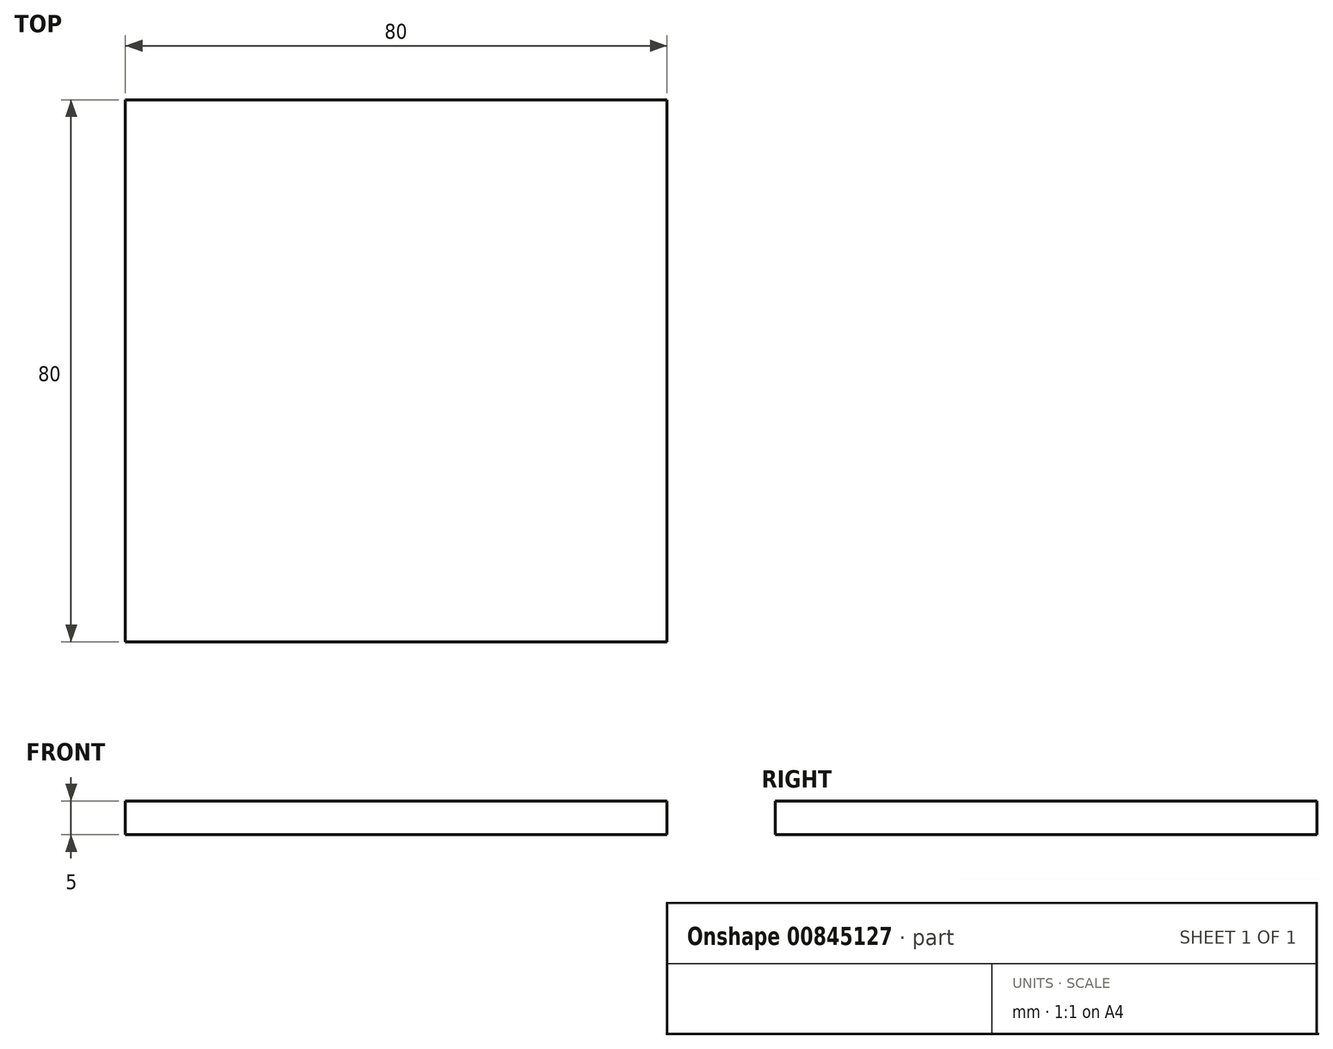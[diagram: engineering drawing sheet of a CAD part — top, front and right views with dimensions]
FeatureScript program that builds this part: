
annotation { "Feature Type Name" : "Feature", "Feature Type Description" : "" }
export const myFeature = defineFeature(function(context is Context, id is Id, definition is map)
    precondition{}
    {
        {
            var Q0;
            Q0=qCreatedBy(makeId("Top.planeOp"),FACE);
            var sketch = newSketch(context, id + "F0", { "sketchPlane" : qUnion([Q0])});
            skLineSegment(sketch, "E0.bottom", {"start": v(0, 0) * mm, "end": v(80, 0) * mm});
            skLineSegment(sketch, "E0.top", {"start": v(0, 80) * mm, "end": v(80, 80) * mm});
            skLineSegment(sketch, "E0.left", {"start": v(0, 0) * mm, "end": v(0, 80) * mm});
            skLineSegment(sketch, "E0.right", {"start": v(80, 0) * mm, "end": v(80, 80) * mm});
            skSolve(sketch);
        }
        {
            var Q0;
            Q0 = qSketchRegion(id + "F0", true);
            extrude(context, id + "F1", {"entities" : qUnion([Q0]), "depth" : 5 * mm, "offsetDistance" : 25 * mm});
        }
    });
